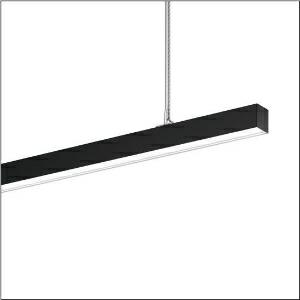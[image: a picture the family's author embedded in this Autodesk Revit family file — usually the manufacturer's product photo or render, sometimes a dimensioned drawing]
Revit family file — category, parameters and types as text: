
# Revit family: silica_21_51mx33tctdb
name_source: partatom
category: Lighting Fixtures
units: mm (PartAtom-declared; Revit-internal decimal feet)

## family parameters
Cut with Voids When Loaded = No
Host = Face
Light Source = No
Part Type = Normal
Room Calculation Point = No
Round Connector Dimension = Use Diameter
Shared = No

## types (1)
- --- (1 x LED, 14340 lm, 134.7 W, 6500K)
    Apparent Load = 135 VA
    CIE Flux Codes = 78 96 99 56 100
    Color Rendering = 80
    Color Temperature = 6500K
    Default Elevation = 1800 mm
    Description = Silica 21, office luminaire, primary optical cover: prismatic diffuser, of PMMA, CAT 2 (L<= 3000cd/m²), light emission: direct/indirect distribution, primary light characteristic: symmetric, installation type: suspended mounting, LED, rated luminous flux: 14.340lm, luminous efficacy: 101lm/W, light colour: 8tw, colour temperature: 2700..6500K, control gear: DALI DT8, with terminal, 3+2-pole, max. 2.5mm², mains connection: 220..240V, AC, 50/60Hz, rated input power: 141.4W, luminaire housing, of aluminium, matt jet black (RAL 9005), length: 3.004mm, width: 53mm, height: 53mm, protection rating (complete): IP20, insulation class (complete): insulation class I (protective earthing), certification: CE, permissible operating ambient temperature: 0..+35°C, standard: EN 50419, packaging unit: 1 piece
    Height = 53 mm
    Lamp = 1 x LED
    Lamp Light Flux = 14340 lm
    Lamp Power = 134.7 W
    Lamp count = 1
    Length = 3004 mm
    Luminous efficacy = 106 lm/W
    Manufacturer = Siteco
    ModVariant = No
    Model = 51MX33TCTDB
    Mounting Place = Ceiling
    Mounting Type = Pendant
    Number of Poles = 1
    OnlyDefault = Yes
    Power Factor = 1
    Product Name = Silica 21
    Product group = office luminaire | ceiling pendant
    ProductGroupID = 903
    Protection Class = Protection class I
    Protection Degree = IP 20
    RLX_Detail_Level = 1
    RLX_Emergency_Light_Flux = 0 lm
    RLX_Emergency_Type = 0
    RLX_Emergency_Type_DB = No
    RlxData = <blob elided: 22821 chars, md5=50a36ab5>
    Socket = socket
    Standby Power = 0 W
    System Light Flux = 14340 lm
    System Power = 135 W
    Type Comments = individual setting
    Type Image = l_1335856.jpg
    URL = http://relux.com
    VarID = @adj_139247
    Voltage = 0 V
    Weight = 0.00 kg
    Width = 53 mm

## geometry (parser evidence)
native form markers: Blend x4, Sweep x12
no freeform markers — native parametric forms only
